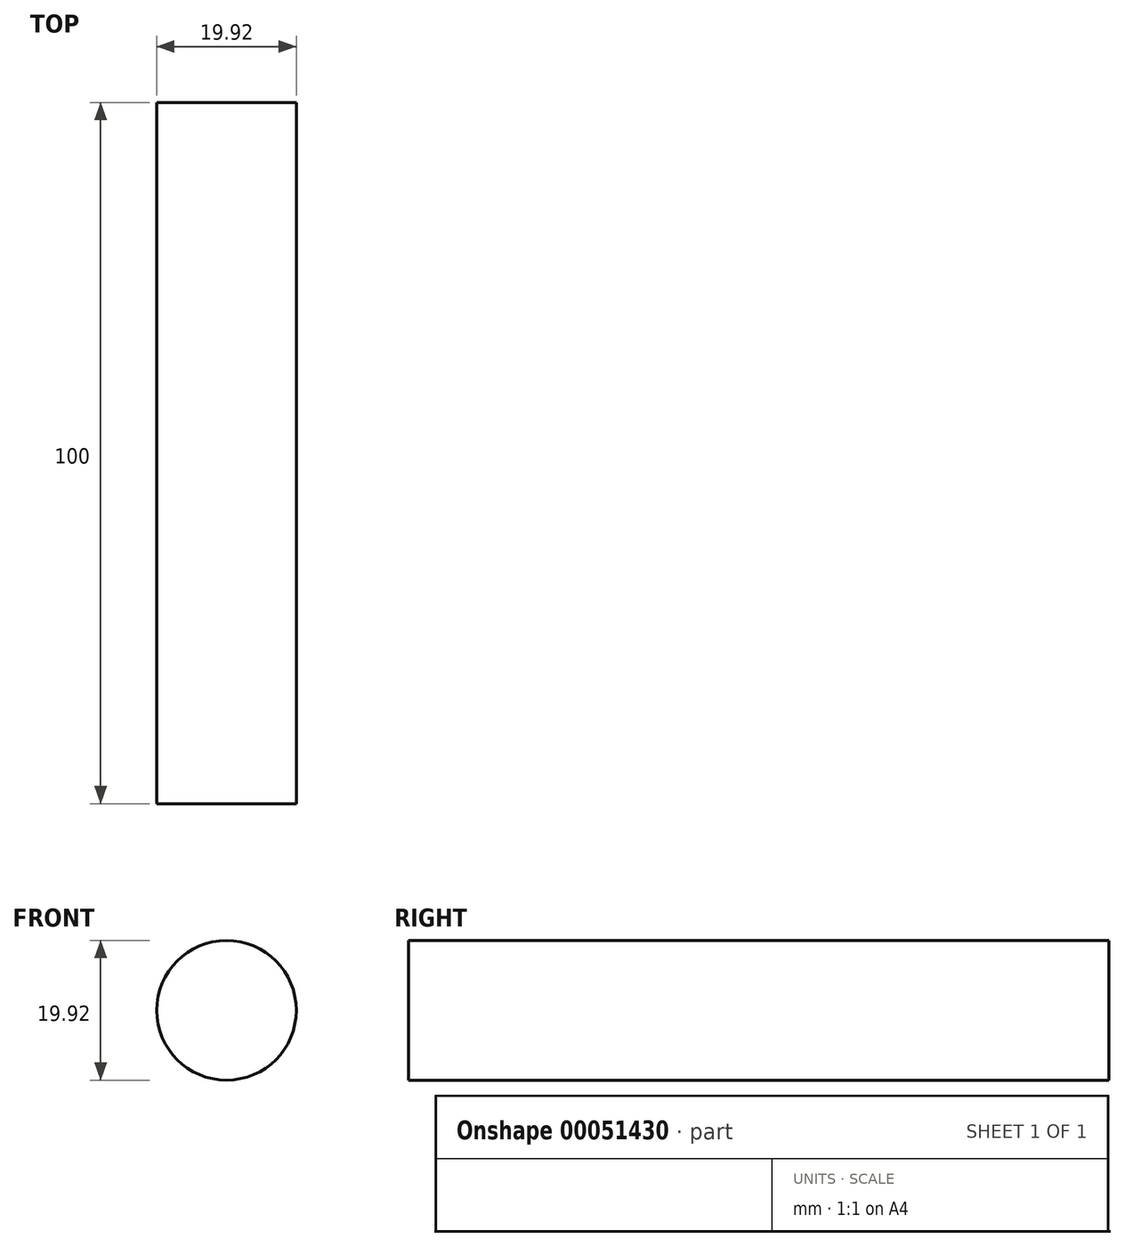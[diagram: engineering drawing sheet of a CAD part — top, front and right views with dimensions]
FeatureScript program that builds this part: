
annotation { "Feature Type Name" : "Feature", "Feature Type Description" : "" }
export const myFeature = defineFeature(function(context is Context, id is Id, definition is map)
    precondition{}
    {
        {
            var Q0;
            Q0=qCreatedBy(makeId("Front.planeOp"),FACE);
            var sketch = newSketch(context, id + "F0", { "sketchPlane" : qUnion([Q0])});
            skCircle(sketch, "E0", {"center": v(0, 0) * mm, "radius": 9.96 * mm});
            skSolve(sketch);
        }
        {
            var Q0;
            Q0=makeQuery(id+"F0.imprint","IMPRINT",FACE,{"disambiguationData":[TD([[makeQuery(id+"F0.imprint","IMPRINT",EDGE,{"derivedFrom":sQuery(id+"F0.wireOp",EDGE,"E0")}),1.0]])]});
            var Q1;
            Q1=sQuery(id+"F0.wireOp",EDGE,"E0");
            extrude(context, id + "F1", {"entities" : qUnion([Q0]), "surfaceEntities" : qUnion([Q1]), "depth" : 100 * mm});
        }
    });
